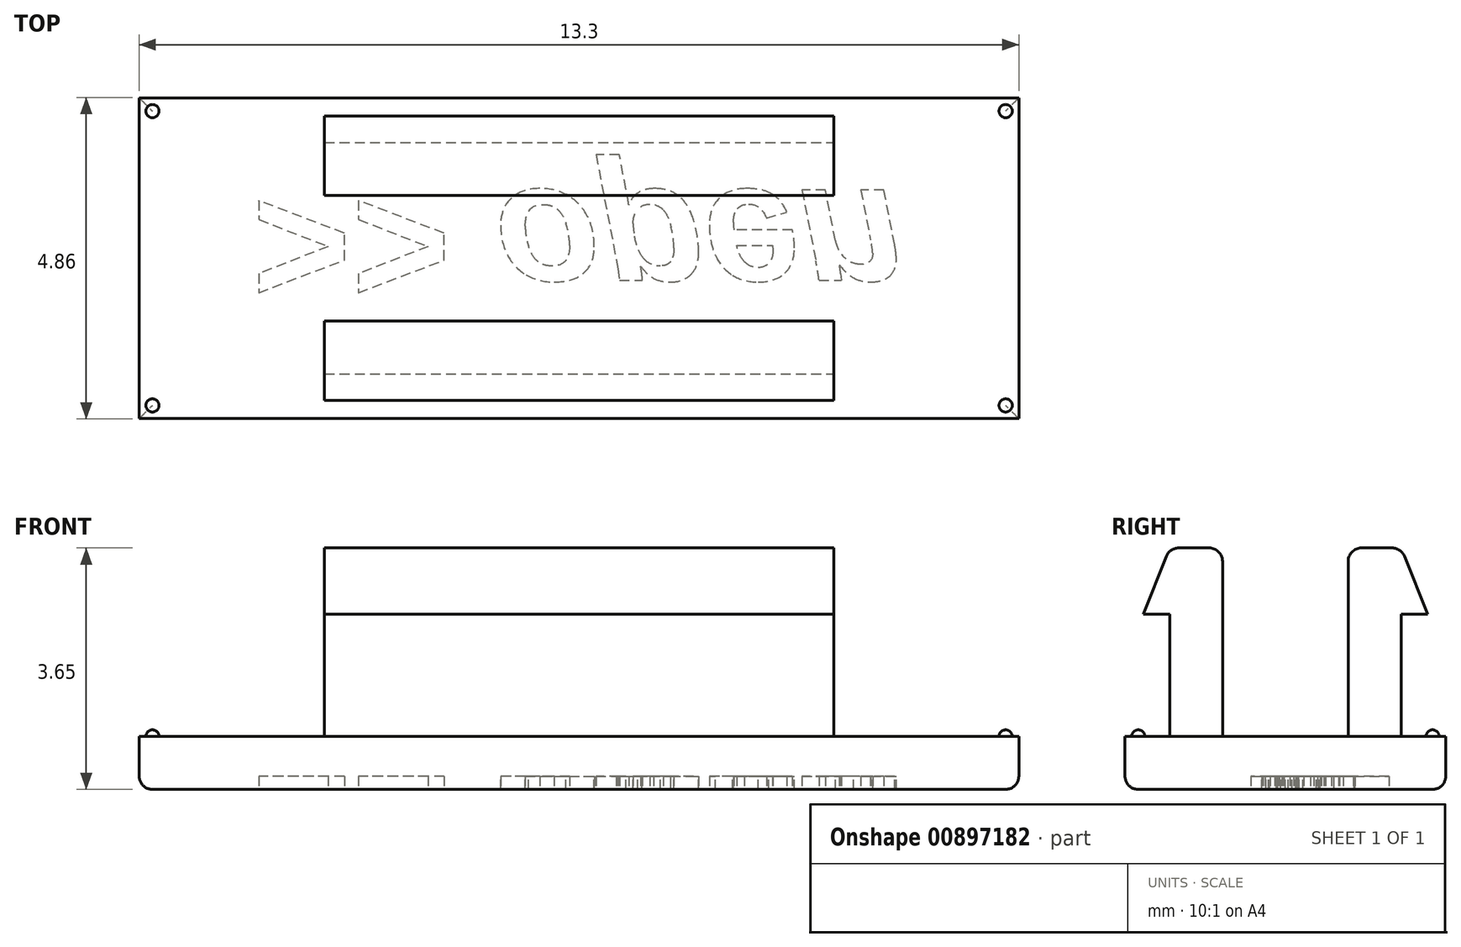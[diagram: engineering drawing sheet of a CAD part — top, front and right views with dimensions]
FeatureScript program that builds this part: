
annotation { "Feature Type Name" : "Feature", "Feature Type Description" : "" }
export const myFeature = defineFeature(function(context is Context, id is Id, definition is map)
    precondition{}
    {
        {
            var Q0;
            Q0=qCreatedBy(makeId("Top.planeOp"),FACE);
            var sketch = newSketch(context, id + "F0", { "sketchPlane" : qUnion([Q0])});
            skLineSegment(sketch, "E0.bottom", {"start": v(6.65, -2.42) * mm, "end": v(-6.65, -2.43) * mm});
            skLineSegment(sketch, "E0.top", {"start": v(6.65, 2.43) * mm, "end": v(-6.65, 2.43) * mm});
            skLineSegment(sketch, "E0.left", {"start": v(6.65, -2.42) * mm, "end": v(6.65, 2.43) * mm});
            skLineSegment(sketch, "E0.right", {"start": v(-6.65, -2.43) * mm, "end": v(-6.65, 2.43) * mm});
            skPoint(sketch, "E0.middle", {"position": v(0, 0) * mm});
            skSolve(sketch);
        }
        {
            var Q0;
            Q0=makeQuery(id+"F0.imprint","IMPRINT",FACE,{"disambiguationData":[TD([[makeQuery(id+"F0.imprint","IMPRINT",EDGE,{"derivedFrom":sQuery(id+"F0.wireOp",EDGE,"E0.bottom")}),-1.0]])]});
            extrude(context, id + "F1", {"entities" : qUnion([Q0]), "depth" : 0.8 * mm, "offsetDistance" : 25 * mm});
        }
        {
            var Q0;
            Q0=makeQuery(id+"F1.opExtrude","CAP_FACE",FACE,{"disambiguationData":[OSD([sQuery(id+"F0.wireOp",EDGE,"E0.bottom"),sQuery(id+"F0.wireOp",EDGE,"E0.top"),sQuery(id+"F0.wireOp",EDGE,"E0.left"),sQuery(id+"F0.wireOp",EDGE,"E0.right")])],"isStart":false});
            var sketch = newSketch(context, id + "F2", { "sketchPlane" : qUnion([Q0])});
            skLineSegment(sketch, "E1.bottom", {"start": v(-3.85, 1.75) * mm, "end": v(3.85, 1.75) * mm});
            skLineSegment(sketch, "E1.top", {"start": v(-3.85, 0.95) * mm, "end": v(3.85, 0.95) * mm});
            skLineSegment(sketch, "E1.left", {"start": v(-3.85, 1.75) * mm, "end": v(-3.85, 0.95) * mm});
            skLineSegment(sketch, "E1.right", {"start": v(3.85, 1.75) * mm, "end": v(3.85, 0.95) * mm});
            skLineSegment(sketch, "E2", {"start": v(6.65, 0) * mm, "end": v(-6.65, 0) * mm, "construction": true});
            skSolve(sketch);
        }
        {
            var Q0;
            Q0=makeQuery(id+"F2.imprint","IMPRINT",FACE,{"disambiguationData":[TD([[makeQuery(id+"F2.imprint","IMPRINT",EDGE,{"derivedFrom":sQuery(id+"F2.wireOp",EDGE,"E1.bottom")}),-1.0]])]});
            extrude(context, id + "F3", {"entities" : qUnion([Q0]), "depth" : 2.85 * mm, "offsetDistance" : 25 * mm});
        }
        {
            var Q0;
            Q0=makeQuery(id+"F3.opExtrude","SWEPT_FACE",FACE,{"disambiguationData":[OSD([sQuery(id+"F2.wireOp",EDGE,"E1.right")])]});
            var sketch = newSketch(context, id + "F4", { "sketchPlane" : qUnion([Q0])});
            skLineSegment(sketch, "E3", {"start": v(1.75, 3.65) * mm, "end": v(1.75, 2.65) * mm});
            skLineSegment(sketch, "E4", {"start": v(1.75, 2.65) * mm, "end": v(2.15, 2.65) * mm});
            skLineSegment(sketch, "E5", {"start": v(2.15, 2.65) * mm, "end": v(1.75, 3.65) * mm});
            skSolve(sketch);
        }
        {
            var Q0;
            Q0=makeQuery(id+"F4.imprint","IMPRINT",FACE,{"disambiguationData":[TD([[makeQuery(id+"F4.imprint","IMPRINT",EDGE,{"derivedFrom":sQuery(id+"F4.wireOp",EDGE,"E3")}),1.0]])]});
            var Q1;
            Q1=makeQuery(id+"F3.opExtrude","SWEPT_FACE",FACE,{"disambiguationData":[OSD([sQuery(id+"F2.wireOp",EDGE,"E1.left")])]});
            extrude(context, id + "F5", {"entities" : qUnion([Q0]), "operationType" : NewBodyOperationType.ADD, "endBound" : BoundingType.UP_TO_SURFACE, "oppositeDirection" : true, "depth" : 25 * mm, "endBoundEntityFace" : qUnion([Q1]), "offsetDistance" : 25 * mm});
        }
        {
            var Q0;
            Q0=makeQuery(id+"F3.opExtrude","SWEPT_BODY",BODY,{"disambiguationData":[OSD([sQuery(id+"F2.wireOp",EDGE,"E1.bottom"),sQuery(id+"F2.wireOp",EDGE,"E1.top"),sQuery(id+"F2.wireOp",EDGE,"E1.left"),sQuery(id+"F2.wireOp",EDGE,"E1.right")])]});
            var Q1;
            Q1=qCreatedBy(makeId("Front.planeOp"),FACE);
            mirror(context, id + "F6", {"entities" : qUnion([Q0]), "mirrorPlane" : qUnion([Q1])});
        }
        {
            var Q0;
            Q0=makeQuery(id+"F1.opExtrude","CAP_FACE",FACE,{"disambiguationData":[OSD([sQuery(id+"F0.wireOp",EDGE,"E0.bottom"),sQuery(id+"F0.wireOp",EDGE,"E0.top"),sQuery(id+"F0.wireOp",EDGE,"E0.left"),sQuery(id+"F0.wireOp",EDGE,"E0.right")])],"isStart":false});
            var sketch = newSketch(context, id + "F7", { "sketchPlane" : qUnion([Q0])});
            skLineSegment(sketch, "E6", {"start": v(-6.45, 2.43) * mm, "end": v(-6.45, -2.43) * mm, "construction": true});
            skLineSegment(sketch, "E7", {"start": v(-6.65, 2.22) * mm, "end": v(6.65, 2.23) * mm, "construction": true});
            skCircle(sketch, "E8", {"center": v(-6.45, 2.22) * mm, "radius": 0.1 * mm});
            skLineSegment(sketch, "E9", {"start": v(-6.65, 0) * mm, "end": v(6.65, 0) * mm, "construction": true});
            skLineSegment(sketch, "E10", {"start": v(0, 2.43) * mm, "end": v(0, -2.42) * mm, "construction": true});
            skSolve(sketch);
        }
        {
            var Q0;
            Q0=makeQuery(id+"F7.imprint","IMPRINT",FACE,{"disambiguationData":[TD([[makeQuery(id+"F7.imprint","IMPRINT",EDGE,{"derivedFrom":sQuery(id+"F7.wireOp",EDGE,"E8")}),1.0]])]});
            extrude(context, id + "F8", {"entities" : qUnion([Q0]), "depth" : 0.1 * mm, "offsetDistance" : 25 * mm});
        }
        {
            var Q0;
            Q0=makeQuery(id+"F8.opExtrude","CAP_FACE",FACE,{"disambiguationData":[OSD([sQuery(id+"F7.wireOp",EDGE,"E8")])],"isStart":false});
            fillet(context, id + "F9", {"entities" : qUnion([Q0]), "radius" : 0.1 * mm, "tangentPropagation" : true, "allowEdgeOverflow" : false});
        }
        {
            var Q0;
            Q0=makeQuery(id+"F8.opExtrude","SWEPT_BODY",BODY,{"disambiguationData":[OSD([sQuery(id+"F7.wireOp",EDGE,"E8")])]});
            var Q1;
            Q1=qCreatedBy(makeId("Front.planeOp"),FACE);
            mirror(context, id + "F10", {"entities" : qUnion([Q0]), "mirrorPlane" : qUnion([Q1])});
        }
        {
            var Q0;
            Q0=makeQuery(id+"F8.opExtrude","SWEPT_BODY",BODY,{"disambiguationData":[OSD([sQuery(id+"F7.wireOp",EDGE,"E8")])]});
            var Q1;
            Q1=makeQuery(id+"F10.opPattern","COPY",BODY,{"derivedFrom":makeQuery(id+"F8.opExtrude","SWEPT_BODY",BODY,{"disambiguationData":[OSD([sQuery(id+"F7.wireOp",EDGE,"E8")])]}),"instanceName":"1"});
            var Q2;
            Q2=qCreatedBy(makeId("Right.planeOp"),FACE);
            mirror(context, id + "F11", {"operationType" : NewBodyOperationType.ADD, "entities" : qUnion([Q0, Q1]), "mirrorPlane" : qUnion([Q2])});
        }
        {
            var Q0;
            Q0=makeQuery(id+"F5.boolean.opBoolean","MERGE",EDGE,{"derivedFrom":[makeQuery(id+"F3.opExtrude","CAP_EDGE",EDGE,{"disambiguationData":[OSD([sQuery(id+"F2.wireOp",EDGE,"E1.bottom")])],"isStart":false}),makeQuery(id+"F5.opExtrude","SWEPT_EDGE",EDGE,{"disambiguationData":[OSD([sQuery(id+"F2.wireOp",EDGE,"E1.right"),sQuery(id+"F4.wireOp",EDGE,"E3"),sQuery(id+"F4.wireOp",EDGE,"E5")])]})]});
            fillet(context, id + "F12", {"entities" : qUnion([Q0]), "radius" : 0.2 * mm, "tangentPropagation" : true, "allowEdgeOverflow" : false});
        }
        {
            var Q0;
            Q0=makeQuery(id+"F6.opPattern","COPY",EDGE,{"derivedFrom":makeQuery(id+"F5.boolean.opBoolean","MERGE",EDGE,{"derivedFrom":[makeQuery(id+"F3.opExtrude","CAP_EDGE",EDGE,{"disambiguationData":[OSD([sQuery(id+"F2.wireOp",EDGE,"E1.bottom")])],"isStart":false}),makeQuery(id+"F5.opExtrude","SWEPT_EDGE",EDGE,{"disambiguationData":[OSD([sQuery(id+"F2.wireOp",EDGE,"E1.right"),sQuery(id+"F4.wireOp",EDGE,"E3"),sQuery(id+"F4.wireOp",EDGE,"E5")])]})]}),"instanceName":"1"});
            fillet(context, id + "F13", {"entities" : qUnion([Q0]), "radius" : 0.2 * mm, "tangentPropagation" : true, "allowEdgeOverflow" : false});
        }
        {
            var Q0;
            Q0=makeQuery(id+"F3.opExtrude","CAP_EDGE",EDGE,{"disambiguationData":[OSD([sQuery(id+"F2.wireOp",EDGE,"E1.top")])],"isStart":false});
            fillet(context, id + "F14", {"entities" : qUnion([Q0]), "radius" : 0.2 * mm, "tangentPropagation" : true, "allowEdgeOverflow" : false});
        }
        {
            var Q0;
            Q0=makeQuery(id+"F6.opPattern","COPY",EDGE,{"derivedFrom":makeQuery(id+"F3.opExtrude","CAP_EDGE",EDGE,{"disambiguationData":[OSD([sQuery(id+"F2.wireOp",EDGE,"E1.top")])],"isStart":false}),"instanceName":"1"});
            fillet(context, id + "F15", {"entities" : qUnion([Q0]), "radius" : 0.2 * mm, "tangentPropagation" : true, "allowEdgeOverflow" : false});
        }
        {
            var Q0;
            Q0=makeQuery(id+"F1.opExtrude","CAP_FACE",FACE,{"disambiguationData":[OSD([sQuery(id+"F0.wireOp",EDGE,"E0.bottom"),sQuery(id+"F0.wireOp",EDGE,"E0.top"),sQuery(id+"F0.wireOp",EDGE,"E0.left"),sQuery(id+"F0.wireOp",EDGE,"E0.right")])],"isStart":true});
            var sketch = newSketch(context, id + "F16", { "sketchPlane" : qUnion([Q0])});
            skText(sketch, "E11", { "text": ">> open", "fontName": "Arimo-BoldItalic.ttf"});
            const initialGuessF16  = {"E11": [-0.005, -0.00103, 1, 0, 0.00186]};
            skSetInitialGuess(sketch, initialGuessF16);
            skSolve(sketch);
        }
        {
            var Q0;
            Q0 = qSketchRegion(id + "F16", true);
            extrude(context, id + "F17", {"entities" : qUnion([Q0]), "operationType" : NewBodyOperationType.REMOVE, "oppositeDirection" : true, "depth" : 0.2 * mm, "offsetDistance" : 25 * mm});
        }
        {
            var Q0;
            Q0=makeQuery(id+"F1.opExtrude","CAP_EDGE",EDGE,{"disambiguationData":[OSD([sQuery(id+"F0.wireOp",EDGE,"E0.right")])],"isStart":true});
            var Q1;
            Q1=makeQuery(id+"F1.opExtrude","CAP_EDGE",EDGE,{"disambiguationData":[OSD([sQuery(id+"F0.wireOp",EDGE,"E0.top")])],"isStart":true});
            var Q2;
            Q2=makeQuery(id+"F1.opExtrude","CAP_EDGE",EDGE,{"disambiguationData":[OSD([sQuery(id+"F0.wireOp",EDGE,"E0.left")])],"isStart":true});
            var Q3;
            Q3=makeQuery(id+"F1.opExtrude","CAP_EDGE",EDGE,{"disambiguationData":[OSD([sQuery(id+"F0.wireOp",EDGE,"E0.bottom")])],"isStart":true});
            fillet(context, id + "F18", {"entities" : qUnion([Q0, Q1, Q2, Q3]), "radius" : 0.2 * mm, "tangentPropagation" : true, "allowEdgeOverflow" : false});
        }
    });
